# Revit family: Faucet-Wall_Mount-Lavatory-KOHLER-Aleo-K-21969IN-1
name_source: partatom
category: Plumbing Fixtures
units: mm (PartAtom-declared; Revit-internal decimal feet)

## family parameters
Cut with Voids When Loaded = No
Host = Face
OmniClass Number = 23.31.11.00
Part Type = Normal
Room Calculation Point = No
Round Connector Dimension = Use Diameter
Shared = No

## types (3) — shared parameters
ADA Compliant = No
Assembly Code = D2010
CW Connection = Yes
Cold Water Inlet = Cold Water Inlet
Date Modified = 08/20/2024
Default Elevation = 36"
Description = Wall mount Lavatory Faucet Trim with Valve
Drain Included = No
Flow Rate = 41 GPM
HW Connection = Yes
Handle Clearance = 3 5/8"
Height = 5 1/4"
Hot Water Inlet = Hot Water Inlet
Length = 6 5/16"
Manufacturer = Kohler Co.
Master Format 2014 = 22 41 39
Master Format 2014 Name = Residential Faucets, Supplies, and Trim
Material = Premium Metal Construction
Pressure = 3.51 psi
Product Name = Aleo
Spout Reach = 6 5/16"
URL = https://www.kohler.co.in
Vent Connection = No
Waste Connection = No
Waste Water Outlet = Waste Water Outlet
WaterSense Certified = No
Width = 7 7/8"

## per-type parameters (varying)
| type | Finish | Model | Product Page URL | Type |
| BV-Brushed Bronze | Kohler-Metal-BV-Brushed_Bronze | K-21969IN-4ND-BV | https://www.kohler.co.in | 1 |
| RGD-Polished Rose Gold | Kohler-Metal-RGD-Polished_Rose_Gold | K-21969IN-4ND-RGD | https://www.kohler.co.in | 2 |
| BRD-Brushed Rose Gold | KOHLER-Metal-BRD-Brushed_Rose_Gold | K-21969IN-4ND-BRD |  | 3 |

## geometry (parser evidence)
native form markers: Sweep x4
no freeform markers — native parametric forms only
